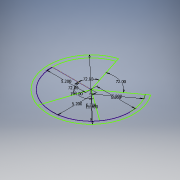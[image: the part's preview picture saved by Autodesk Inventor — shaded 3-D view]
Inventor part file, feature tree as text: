
AUTODESK INVENTOR PART (.ipt)
format: ipt  version: 2017 (Build 210142000, 142)  size: 98,816 bytes
history: native  units: in
note: dims shown in document units (in); Inventor stores cm internally (conversion verified against a paired STEP export)
features: sketch x1
ambient origin geometry x8: Origin, YZ Plane, XZ Plane, XY Plane, X Axis, Y Axis, Z Axis, Center Point
feature tree (1):
  sketch  "Sketch1"  dims[d0=5.2in d1=5.2in d2=5.2in d3=5.2in d4=5.2in d8=0.9895in d13=11.4in d14=0.4947in d15=0.4947in d16=0.4947in]
